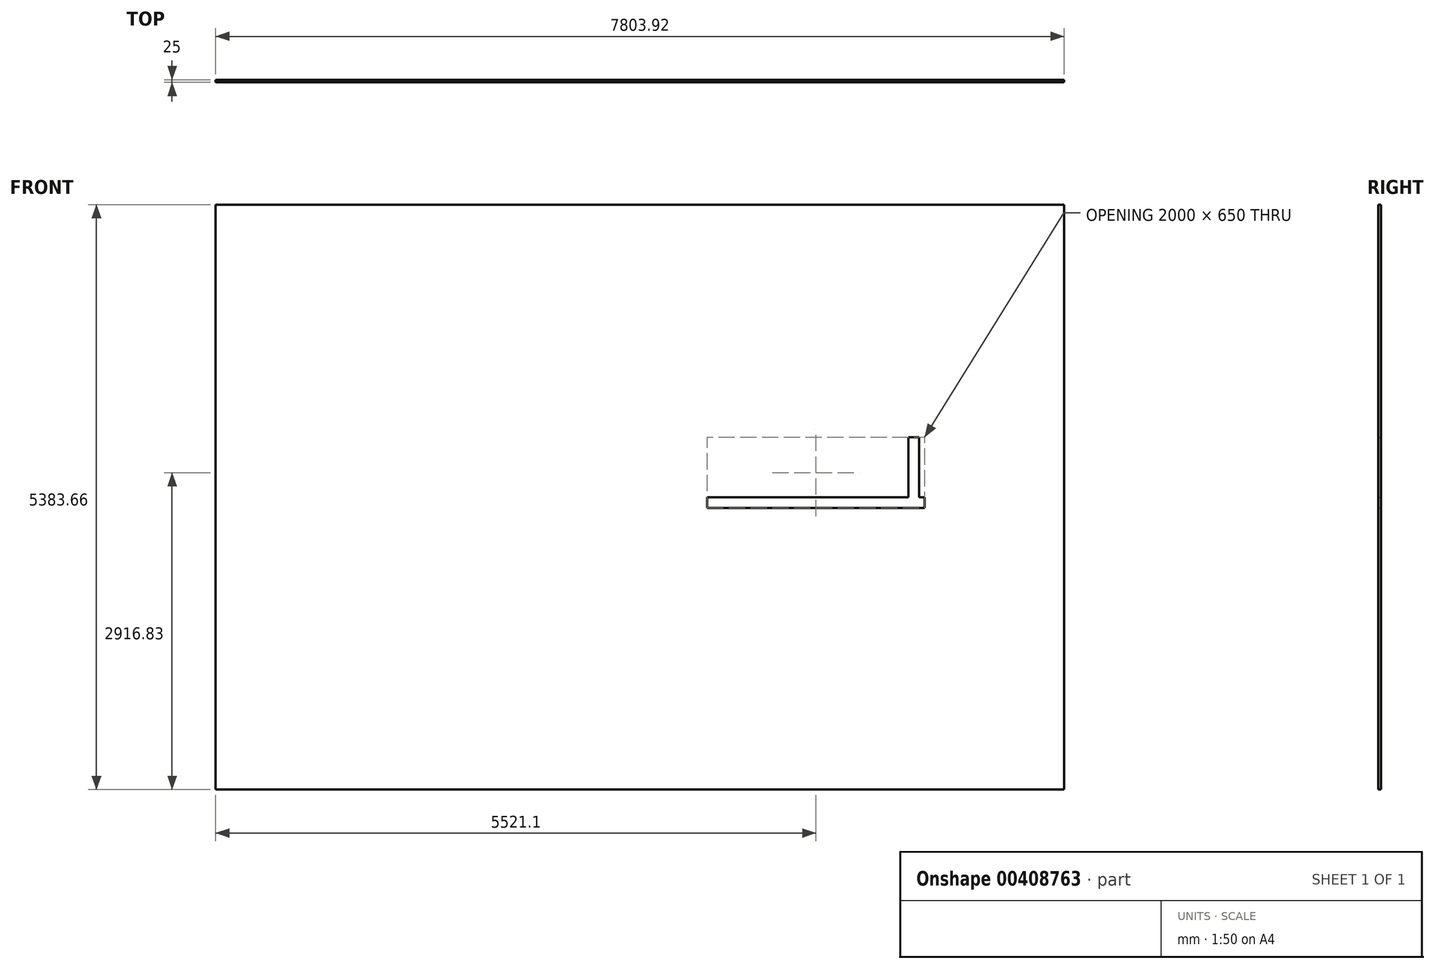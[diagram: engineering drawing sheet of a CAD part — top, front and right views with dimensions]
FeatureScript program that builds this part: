
annotation { "Feature Type Name" : "Feature", "Feature Type Description" : "" }
export const myFeature = defineFeature(function(context is Context, id is Id, definition is map)
    precondition{}
    {
        {
            var Q0;
            Q0=qCreatedBy(makeId("Front.planeOp"),FACE);
            var sketch = newSketch(context, id + "F0", { "sketchPlane" : qUnion([Q0])});
            skLineSegment(sketch, "E0.bottom", {"start": v(1000, 50) * mm, "end": v(-1000, 50) * mm});
            skLineSegment(sketch, "E0.top", {"start": v(1000, -50) * mm, "end": v(-1000, -50) * mm});
            skLineSegment(sketch, "E0.left", {"start": v(1000, 50) * mm, "end": v(1000, -50) * mm});
            skLineSegment(sketch, "E0.right", {"start": v(-1000, 50) * mm, "end": v(-1000, -50) * mm});
            skPoint(sketch, "E0.middle", {"position": v(0, 0) * mm});
            skLineSegment(sketch, "E1.bottom", {"start": v(2282.82, -2641.83) * mm, "end": v(-5521.1, -2641.83) * mm});
            skLineSegment(sketch, "E1.top", {"start": v(2282.82, 2741.83) * mm, "end": v(-5521.1, 2741.83) * mm});
            skLineSegment(sketch, "E1.left", {"start": v(2282.82, -2641.83) * mm, "end": v(2282.82, 2741.83) * mm});
            skLineSegment(sketch, "E1.right", {"start": v(-5521.1, -2641.83) * mm, "end": v(-5521.1, 2741.83) * mm});
            skPoint(sketch, "E1.middle", {"position": v(-1619.14, 50) * mm});
            skLineSegment(sketch, "E2.bottom", {"start": v(950, 50) * mm, "end": v(850, 50) * mm});
            skLineSegment(sketch, "E2.top", {"start": v(950, 600) * mm, "end": v(850, 600) * mm});
            skLineSegment(sketch, "E2.left", {"start": v(950, 50) * mm, "end": v(950, 600) * mm});
            skLineSegment(sketch, "E2.right", {"start": v(850, 50) * mm, "end": v(850, 600) * mm});
            skLineSegment(sketch, "E3", {"start": v(0, 50) * mm, "end": v(0, -50) * mm, "construction": true});
            skSolve(sketch);
        }
        {
            var Q0;
            Q0 = qSketchRegion(id + "F0", true);
            extrude(context, id + "F1", {"entities" : qUnion([Q0]), "depth" : 25 * mm, "offsetDistance" : 25 * mm});
        }
    });
